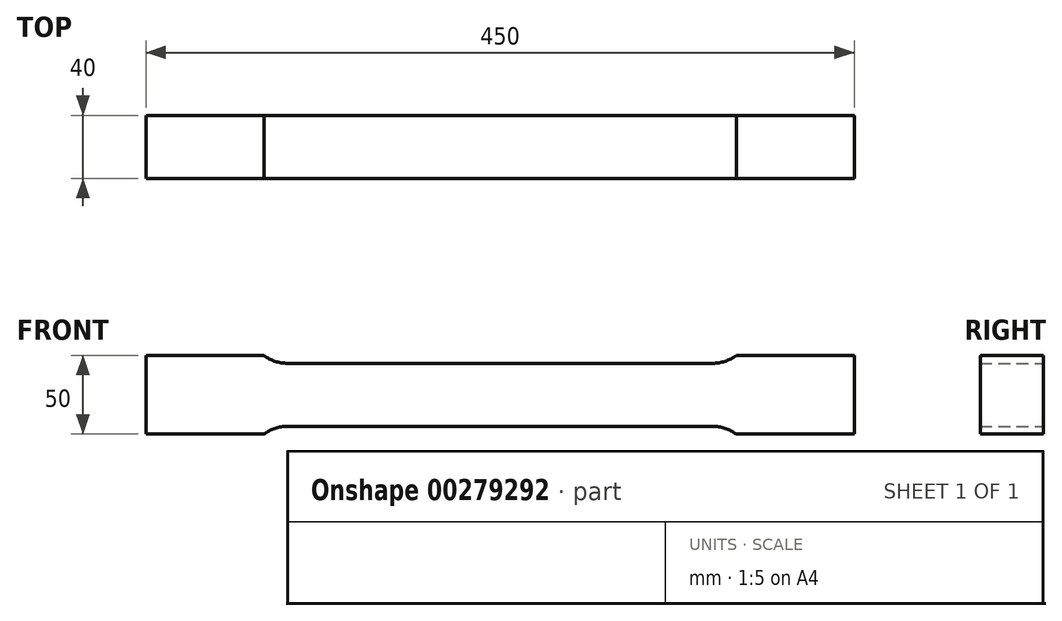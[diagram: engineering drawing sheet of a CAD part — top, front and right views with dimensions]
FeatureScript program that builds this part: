
annotation { "Feature Type Name" : "Feature", "Feature Type Description" : "" }
export const myFeature = defineFeature(function(context is Context, id is Id, definition is map)
    precondition{}
    {
        {
            var Q0;
            Q0=qCreatedBy(makeId("Front.planeOp"),FACE);
            var sketch = newSketch(context, id + "F0", { "sketchPlane" : qUnion([Q0])});
            skLineSegment(sketch, "E0", {"start": v(0, 20) * mm, "end": v(135, 20) * mm});
            skArc(sketch, "E1", {"start": v(135, 20) * mm, "mid": v(142.9, 21.28) * mm, "end": v(150, 25) * mm});
            skLineSegment(sketch, "E2", {"start": v(150, 25) * mm, "end": v(225, 25) * mm});
            skLineSegment(sketch, "E3", {"start": v(225, 25) * mm, "end": v(225, 0) * mm});
            skLineSegment(sketch, "E4.MirrorCS", {"start": v(0, -20) * mm, "end": v(135, -20) * mm});
            skLineSegment(sketch, "E5.MirrorCS", {"start": v(225, -25) * mm, "end": v(225, 0) * mm});
            skLineSegment(sketch, "E6.MirrorCS", {"start": v(150, -25) * mm, "end": v(225, -25) * mm});
            skArc(sketch, "E7.MirrorCS", {"start": v(135, -20) * mm, "mid": v(142.9, -21.28) * mm, "end": v(150, -25) * mm});
            skArc(sketch, "E8.MirrorCS", {"start": v(-135, -20) * mm, "mid": v(-142.9, -21.28) * mm, "end": v(-150, -25) * mm});
            skLineSegment(sketch, "E9.MirrorCS", {"start": v(-150, -25) * mm, "end": v(-225, -25) * mm});
            skLineSegment(sketch, "E10.MirrorCS", {"start": v(0, 20) * mm, "end": v(-135, 20) * mm});
            skArc(sketch, "E11.MirrorCS", {"start": v(-135, 20) * mm, "mid": v(-142.9, 21.28) * mm, "end": v(-150, 25) * mm});
            skLineSegment(sketch, "E12.MirrorCS", {"start": v(-150, 25) * mm, "end": v(-225, 25) * mm});
            skLineSegment(sketch, "E13.MirrorCS", {"start": v(-225, -25) * mm, "end": v(-225, 0) * mm});
            skLineSegment(sketch, "E14.MirrorCS", {"start": v(-225, 25) * mm, "end": v(-225, 0) * mm});
            skLineSegment(sketch, "E15.MirrorCS", {"start": v(0, -20) * mm, "end": v(-135, -20) * mm});
            skSolve(sketch);
        }
        {
            var Q0;
            Q0 = qSketchRegion(id + "F0", true);
            extrude(context, id + "F1", {"entities" : qUnion([Q0]), "endBound" : BoundingType.SYMMETRIC, "depth" : 40 * mm});
        }
    });
